MODEL slx_9bdd1c21e4de
CONFIG AbsTol = auto
CONFIG EnableMultiTasking = off
CONFIG FixedStep = auto
CONFIG MaxStep = auto
CONFIG MinStep = auto
CONFIG RelTol = 1e-3
CONFIG SampleTimeConstraint = Unconstrained
CONFIG SolverName = VariableStepAuto
CONFIG StartTime = 0.0
CONFIG StopTime = 0.2
BLOCK [Reference] AC Voltage Source  REF=spsACVoltageSourceLib/AC Voltage Source
  LibrarySourceBlock = sps_lib/Sources/AC Voltage Source
  NameLocation = left
  SourceBlock = spsACVoltageSourceLib/AC Voltage Source
  SourceType = AC Voltage Source
BLOCK [Reference] Current Measurement  REF=spsCurrentMeasurementLib/Current Measurement
  LibrarySourceBlock = sps_lib/Sensors and Measurements/Current Measurement
  SourceBlock = spsCurrentMeasurementLib/Current Measurement
  SourceType = Current Measurement
  UserDataPersistent = on
BLOCK [Reference] Current Measurement1  REF=spsCurrentMeasurementLib/Current Measurement
  LibrarySourceBlock = sps_lib/Sensors and Measurements/Current Measurement
  SourceBlock = spsCurrentMeasurementLib/Current Measurement
  SourceType = Current Measurement
  UserDataPersistent = on
BLOCK [Reference] Diode  REF=spsDiodeLib/Diode
  LibrarySourceBlock = sps_lib/Power Electronics/Diode
  NameLocation = right
  SourceBlock = spsDiodeLib/Diode
  SourceType = Diode
BLOCK [Reference] Diode1  REF=spsDiodeLib/Diode
  LibrarySourceBlock = sps_lib/Power Electronics/Diode
  NameLocation = right
  SourceBlock = spsDiodeLib/Diode
  SourceType = Diode
BLOCK [Reference] Diode2  REF=spsDiodeLib/Diode
  LibrarySourceBlock = sps_lib/Power Electronics/Diode
  NameLocation = right
  SourceBlock = spsDiodeLib/Diode
  SourceType = Diode
BLOCK [Reference] Diode3  REF=spsDiodeLib/Diode
  LibrarySourceBlock = sps_lib/Power Electronics/Diode
  NameLocation = right
  SourceBlock = spsDiodeLib/Diode
  SourceType = Diode
BLOCK [Display] Display
  Decimation = 1
BLOCK [Reference] Ground  REF=spsGroundLib/Ground
  LibrarySourceBlock = sps_lib/Utilities/Ground
  NameLocation = right
  SourceBlock = spsGroundLib/Ground
  SourceType = Ground
BLOCK [Reference] Mean  REF=spsMeanLib/Mean
  LibrarySourceBlock = sps_lib/Sensors and Measurements/Mean
  SourceBlock = spsMeanLib/Mean
  SourceType = Mean
BLOCK [Scope] Scope
  ActiveDisplayYMaximum = 337.54342885565359
  ActiveDisplayYMinimum = -37.504825428405944
  Floating = off
  GraphicalSettings = {"Style":{"BackgroundColor":[0.12941176470588237,0.12941176470588237,0.12941176470588237],"AxesColor":[0.07058823529411765,0.07058823529411765,0.07058823529411765],"LabelsColor":[0.8509803921568627,0.8509803921568627,0.8509803921568627],"PreserveColors":false,"Visible":[true],"LineStyle":["-"],"LineWidth":[1.5],"BarWidth":[0.9],"LineColor":["auto"],"LineFaceAlpha":[1],"LineEdgeAlpha":[1],"Marker":...<+2019ch>
  MultipleDisplayCache = [{"MaxYLimMag":337.54342885565359,"MaxYLimReal":337.54342885565359,"MinYLimMag":0,"MinYLimReal":-37.504825428405944,"PlotAsMagnitudePhase":false,"ShowGrid":true,"ShowLegend":false,"Title":"%<SignalLabel>","YLabel":""}]
  NumInputPorts = 1
  ScopeFrameLocation = window
  WasSavedAsWebScope = on
  WindowPosition = [0.000000,32.000000,1536.000000,801.000000,]
BLOCK [Scope] Scope1
  ActiveDisplayYMaximum = 164.29455570774294
  ActiveDisplayYMinimum = -40.6124656236994
  DataLoggingVariableName = ScopeData1
  Floating = off
  GraphicalSettings = {"Style":{"BackgroundColor":[0.12941176470588237,0.12941176470588237,0.12941176470588237],"AxesColor":[0.07058823529411765,0.07058823529411765,0.07058823529411765],"LabelsColor":[0.8509803921568627,0.8509803921568627,0.8509803921568627],"PreserveColors":false,"Visible":[true],"LineStyle":["-"],"LineWidth":[1.5],"BarWidth":[0.9],"LineColor":["auto"],"LineFaceAlpha":[1],"LineEdgeAlpha":[1],"Marker":...<+2019ch>
  MultipleDisplayCache = [{"MaxYLimMag":164.29455570774294,"MaxYLimReal":164.29455570774294,"MinYLimMag":0,"MinYLimReal":-40.6124656236994,"PlotAsMagnitudePhase":false,"ShowGrid":true,"ShowLegend":false,"Title":"%<SignalLabel>","YLabel":""}]
  NameLocation = right
  NumInputPorts = 1
  ScopeFrameLocation = window
  WasSavedAsWebScope = on
  WindowPosition = [1.000000,41.000000,1536.000000,801.000000,]
BLOCK [Scope] Scope2
  ActiveDisplayYMaximum = 126.52753162504482
  ActiveDisplayYMinimum = -236.61883350471254
  DataLoggingVariableName = ScopeData2
  Floating = off
  GraphicalSettings = {"Style":{"BackgroundColor":[0.12941176470588237,0.12941176470588237,0.12941176470588237],"AxesColor":[0.07058823529411765,0.07058823529411765,0.07058823529411765],"LabelsColor":[0.8509803921568627,0.8509803921568627,0.8509803921568627],"PreserveColors":false,"Visible":[true,true],"LineStyle":["-","-"],"LineWidth":[1.5,1.5],"BarWidth":[0.9,0.9],"LineColor":["auto","auto"],"LineFaceAlpha":[1,1],"Li...<+2166ch>
  MultipleDisplayCache = [{"MaxYLimMag":236.61883350471254,"MaxYLimReal":126.52753162504482,"MinYLimMag":0,"MinYLimReal":-236.61883350471254,"PlotAsMagnitudePhase":false,"ShowGrid":true,"ShowLegend":false,"Title":"%<SignalLabel>","YLabel":""}]
  NameLocation = right
  NumInputPorts = 1
  ScopeFrameLocation = window
  WasSavedAsWebScope = on
  WindowPosition = [488.000000,222.000000,560.000000,420.000000,]
BLOCK [Scope] Scope3
  ActiveDisplayYMaximum = 191.64559463687868
  ActiveDisplayYMinimum = -287.00698047954393
  DataLoggingVariableName = ScopeData3
  Floating = off
  GraphicalSettings = {"Style":{"BackgroundColor":[0.12941176470588237,0.12941176470588237,0.12941176470588237],"AxesColor":[0.07058823529411765,0.07058823529411765,0.07058823529411765],"LabelsColor":[0.8509803921568627,0.8509803921568627,0.8509803921568627],"PreserveColors":false,"Visible":[true,true],"LineStyle":["-","-"],"LineWidth":[1.5,1.5],"BarWidth":[0.9,0.9],"LineColor":["auto","auto"],"LineFaceAlpha":[1,1],"Li...<+2158ch>
  MultipleDisplayCache = [{"MaxYLimMag":287.00698047954393,"MaxYLimReal":191.64559463687868,"MinYLimMag":0,"MinYLimReal":-287.00698047954393,"PlotAsMagnitudePhase":false,"ShowGrid":true,"ShowLegend":false,"Title":"%<SignalLabel>","YLabel":""}]
  NameLocation = right
  NumInputPorts = 1
  ScopeFrameLocation = window
  WasSavedAsWebScope = on
  WindowPosition = [488.000000,222.000000,560.000000,420.000000,]
BLOCK [Scope] Scope4
  ActiveDisplayYMaximum = 126.52753162504482
  ActiveDisplayYMinimum = -236.61883350471254
  DataLoggingVariableName = ScopeData4
  Floating = off
  GraphicalSettings = {"Style":{"BackgroundColor":[0.12941176470588237,0.12941176470588237,0.12941176470588237],"AxesColor":[0.07058823529411765,0.07058823529411765,0.07058823529411765],"LabelsColor":[0.8509803921568627,0.8509803921568627,0.8509803921568627],"PreserveColors":false,"Visible":[true,true],"LineStyle":["-","-"],"LineWidth":[1.5,1.5],"BarWidth":[0.9,0.9],"LineColor":["auto","auto"],"LineFaceAlpha":[1,1],"Li...<+2166ch>
  MultipleDisplayCache = [{"MaxYLimMag":236.61883350471254,"MaxYLimReal":126.52753162504482,"MinYLimMag":0,"MinYLimReal":-236.61883350471254,"PlotAsMagnitudePhase":false,"ShowGrid":true,"ShowLegend":false,"Title":"%<SignalLabel>","YLabel":""}]
  NameLocation = right
  NumInputPorts = 1
  ScopeFrameLocation = window
  WasSavedAsWebScope = on
  WindowPosition = [488.000000,222.000000,560.000000,420.000000,]
BLOCK [Scope] Scope5
  ActiveDisplayYMaximum = 847.43866821622464
  ActiveDisplayYMinimum = -317.56132708157151
  DataLoggingVariableName = ScopeData5
  Floating = off
  GraphicalSettings = {"Style":{"BackgroundColor":[0.12941176470588237,0.12941176470588237,0.12941176470588237],"AxesColor":[0.07058823529411765,0.07058823529411765,0.07058823529411765],"LabelsColor":[0.8509803921568627,0.8509803921568627,0.8509803921568627],"PreserveColors":false,"Visible":[true,true],"LineStyle":["-","-"],"LineWidth":[1.5,1.5],"BarWidth":[0.9,0.9],"LineColor":["auto","auto"],"LineFaceAlpha":[1,1],"Li...<+2160ch>
  MultipleDisplayCache = [{"MaxYLimMag":847.43866821622464,"MaxYLimReal":847.43866821622464,"MinYLimMag":0,"MinYLimReal":-317.56132708157151,"PlotAsMagnitudePhase":false,"ShowGrid":true,"ShowLegend":false,"Title":"%<SignalLabel>","YLabel":""}]
  NameLocation = right
  NumInputPorts = 1
  ScopeFrameLocation = window
  WasSavedAsWebScope = on
  WindowPosition = [488.000000,222.000000,560.000000,420.000000,]
BLOCK [Scope] Scope6
  ActiveDisplayYMaximum = 161.72667079451179
  ActiveDisplayYMinimum = -17.970873212055253
  DataLoggingVariableName = ScopeData6
  Floating = off
  GraphicalSettings = {"Style":{"BackgroundColor":[0.12941176470588237,0.12941176470588237,0.12941176470588237],"AxesColor":[0.07058823529411765,0.07058823529411765,0.07058823529411765],"LabelsColor":[0.8509803921568627,0.8509803921568627,0.8509803921568627],"PreserveColors":false,"Visible":[true],"LineStyle":["-"],"LineWidth":[1.5],"BarWidth":[0.9],"LineColor":["auto"],"LineFaceAlpha":[1],"LineEdgeAlpha":[1],"Marker":...<+2021ch>
  MultipleDisplayCache = [{"MaxYLimMag":161.72667079451179,"MaxYLimReal":161.72667079451179,"MinYLimMag":0,"MinYLimReal":-17.970873212055253,"PlotAsMagnitudePhase":false,"ShowGrid":true,"ShowLegend":false,"Title":"%<SignalLabel>","YLabel":""}]
  NameLocation = right
  NumInputPorts = 1
  ScopeFrameLocation = window
  WasSavedAsWebScope = on
  WindowPosition = [0.000000,32.000000,1536.000000,801.000000,]
BLOCK [Reference] Series RLC Branch  REF=spsSeriesRLCBranchLib/Series RLC Branch
  LibrarySourceBlock = sps_lib/Passives/Series RLC Branch
  NameLocation = left
  SourceBlock = spsSeriesRLCBranchLib/Series RLC Branch
  SourceType = Series RLC Branch
BLOCK [Reference] Series RLC Branch1  REF=spsSeriesRLCBranchLib/Series RLC Branch
  LibrarySourceBlock = sps_lib/Passives/Series RLC Branch
  NameLocation = left
  SourceBlock = spsSeriesRLCBranchLib/Series RLC Branch
  SourceType = Series RLC Branch
BLOCK [Reference] Series RLC Branch2  REF=spsSeriesRLCBranchLib/Series RLC Branch
  LibrarySourceBlock = sps_lib/Passives/Series RLC Branch
  SourceBlock = spsSeriesRLCBranchLib/Series RLC Branch
  SourceType = Series RLC Branch
BLOCK [Reference] Voltage Measurement  REF=spsVoltageMeasurementLib/Voltage Measurement
  LibrarySourceBlock = sps_lib/Sensors and Measurements/Voltage Measurement
  SourceBlock = spsVoltageMeasurementLib/Voltage Measurement
  SourceType = Voltage Measurement
  UserDataPersistent = on
BLOCK [Reference] powergui  REF=sps_lib/powergui
  LibrarySourceBlock = sps_lib/powergui
  Priority = 1
  SourceBlock = sps_lib/powergui
  SourceType = PSB option menu block
LINE Current Measurement1:1 -> Scope6:1
LINE Current Measurement:1 -> Scope1:1
LINE Current Measurement:lconn -> Series RLC Branch2:rconn
LINE Diode1:1 -> Scope2:1
LINE Diode2:1 -> Scope4:1
LINE Diode3:1 -> Scope5:1
LINE Diode:1 -> Scope3:1
LINE Mean:1 -> Display:1
LINE Series RLC Branch2:lconn -> AC Voltage Source:rconn
LINE Voltage Measurement:1 -> Mean:1
LINE Voltage Measurement:1 -> Scope:1
